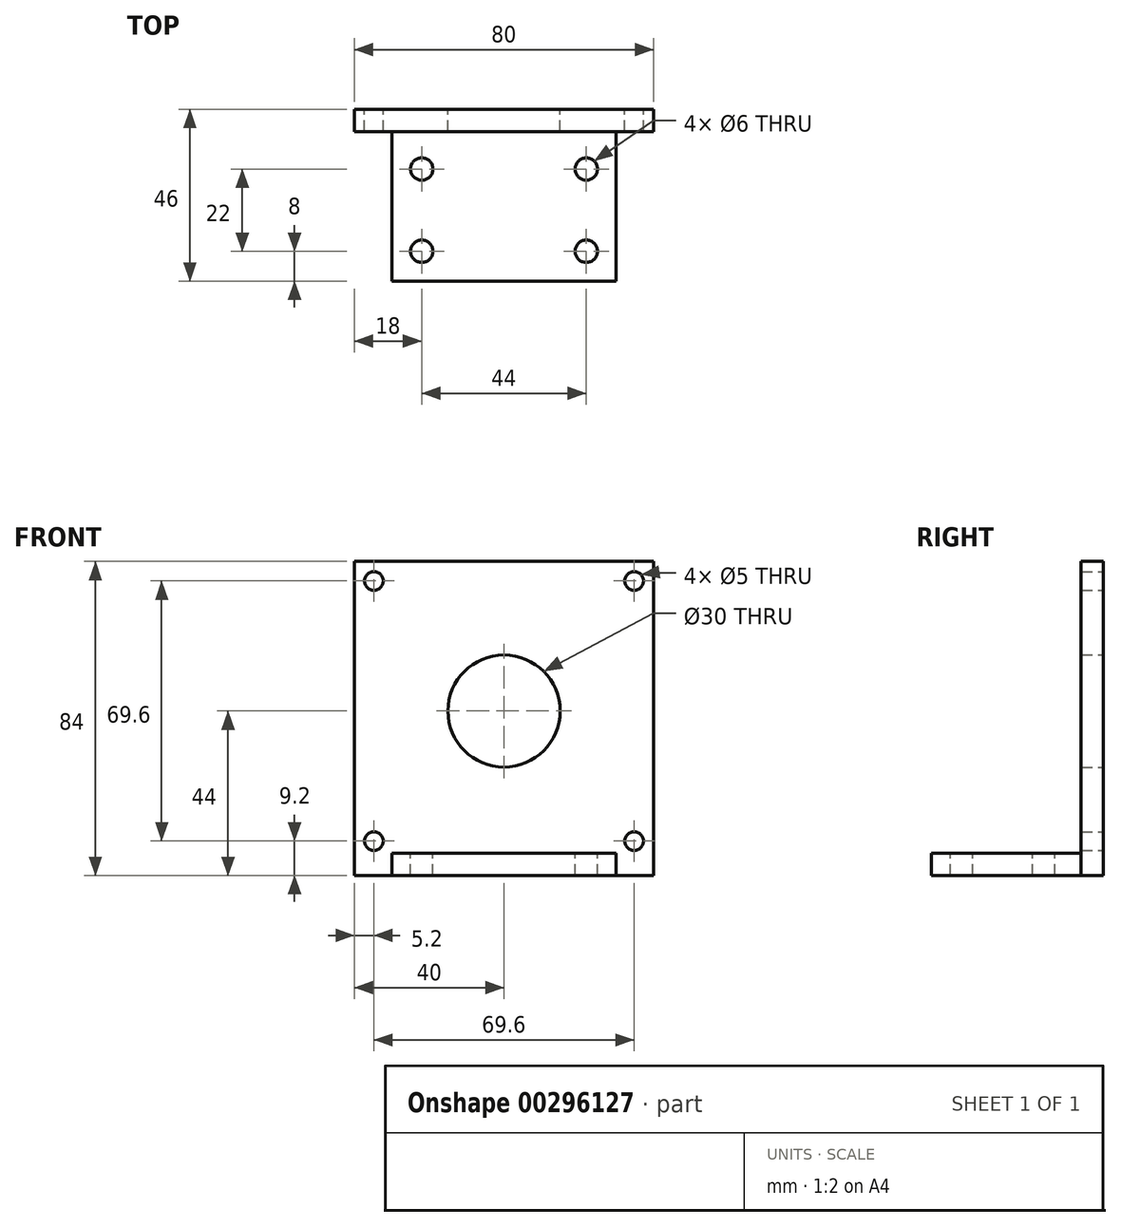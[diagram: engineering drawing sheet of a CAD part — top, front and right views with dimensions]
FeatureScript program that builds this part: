
annotation { "Feature Type Name" : "Feature", "Feature Type Description" : "" }
export const myFeature = defineFeature(function(context is Context, id is Id, definition is map)
    precondition{}
    {
        {
            var Q0;
            Q0=qCreatedBy(makeId("Front.planeOp"),FACE);
            var sketch = newSketch(context, id + "F0", { "sketchPlane" : qUnion([Q0])});
            skLineSegment(sketch, "E0.bottom", {"start": v(-40, 40) * mm, "end": v(40, 40) * mm});
            skLineSegment(sketch, "E0.top", {"start": v(-40, -40) * mm, "end": v(40, -40) * mm});
            skLineSegment(sketch, "E0.left", {"start": v(-40, 40) * mm, "end": v(-40, -40) * mm});
            skLineSegment(sketch, "E0.right", {"start": v(40, 40) * mm, "end": v(40, -40) * mm});
            skPoint(sketch, "E0.middle", {"position": v(0, 0) * mm});
            skLineSegment(sketch, "E1.bottom", {"start": v(-34.8, 34.8) * mm, "end": v(34.8, 34.8) * mm, "construction": true});
            skLineSegment(sketch, "E1.top", {"start": v(-34.8, -34.8) * mm, "end": v(34.8, -34.8) * mm, "construction": true});
            skLineSegment(sketch, "E1.left", {"start": v(-34.8, 34.8) * mm, "end": v(-34.8, -34.8) * mm, "construction": true});
            skLineSegment(sketch, "E1.right", {"start": v(34.8, 34.8) * mm, "end": v(34.8, -34.8) * mm, "construction": true});
            skCircle(sketch, "E2", {"center": v(-34.8, 34.8) * mm, "radius": 2.5 * mm});
            skCircle(sketch, "E3", {"center": v(34.8, 34.8) * mm, "radius": 2.5 * mm});
            skCircle(sketch, "E4", {"center": v(34.8, -34.8) * mm, "radius": 2.5 * mm});
            skCircle(sketch, "E5", {"center": v(-34.8, -34.8) * mm, "radius": 2.5 * mm});
            skCircle(sketch, "E6", {"center": v(0, 0) * mm, "radius": 15 * mm});
            skSolve(sketch);
        }
        {
            var Q0;
            Q0=qSketchRegion(id+"F0",true);
            extrude(context, id + "F1", {"entities" : qUnion([Q0]), "depth" : 6 * mm, "offsetDistance" : 25 * mm});
        }
        {
            var Q0;
            Q0=makeQuery(id+"F1.opExtrude","CAP_FACE",FACE,{"disambiguationData":[OSD([sQuery(id+"F0.wireOp",EDGE,"E0.bottom"),sQuery(id+"F0.wireOp",EDGE,"E0.top"),sQuery(id+"F0.wireOp",EDGE,"E0.left"),sQuery(id+"F0.wireOp",EDGE,"E0.right"),sQuery(id+"F0.wireOp",EDGE,"E2"),sQuery(id+"F0.wireOp",EDGE,"E3"),sQuery(id+"F0.wireOp",EDGE,"E4"),sQuery(id+"F0.wireOp",EDGE,"E5"),sQuery(id+"F0.wireOp",EDGE,"E6")])],"isStart":false});
            var sketch = newSketch(context, id + "F2", { "sketchPlane" : qUnion([Q0])});
            skLineSegment(sketch, "E7.bottom", {"start": v(-30, -38) * mm, "end": v(30, -38) * mm});
            skLineSegment(sketch, "E7.top", {"start": v(-30, -44) * mm, "end": v(30, -44) * mm});
            skLineSegment(sketch, "E7.left", {"start": v(-30, -38) * mm, "end": v(-30, -44) * mm});
            skLineSegment(sketch, "E7.right", {"start": v(30, -38) * mm, "end": v(30, -44) * mm});
            skSolve(sketch);
        }
        {
            var Q0;
            Q0=makeQuery(id+"F2.imprint","IMPRINT",FACE,{"disambiguationData":[TD([[makeQuery(id+"F2.imprint","IMPRINT",EDGE,{"derivedFrom":sQuery(id+"F2.wireOp",EDGE,"E7.bottom")}),-1.0]])]});
            var Q1;
            {var subQ0=sQuery(id+"F2.wireOp",EDGE,"E7.top");Q1=makeQuery(id+"F2.imprint","IMPRINT",FACE,{"disambiguationData":[TD([[makeQuery(id+"F2.imprint","IMPRINT",EDGE,{"derivedFrom":subQ0}),1.0]])]});}
            extrude(context, id + "F3", {"entities" : qUnion([Q0, Q1]), "operationType" : NewBodyOperationType.ADD, "depth" : 40 * mm, "offsetDistance" : 25 * mm});
        }
        {
            var Q0;
            Q0=makeQuery(id+"F3.opExtrude","SWEPT_FACE",FACE,{"disambiguationData":[OSD([sQuery(id+"F2.wireOp",EDGE,"E7.bottom")])]});
            var sketch = newSketch(context, id + "F4", { "sketchPlane" : qUnion([Q0])});
            skLineSegment(sketch, "E8.bottom", {"start": v(-22, -38) * mm, "end": v(22, -38) * mm, "construction": true});
            skLineSegment(sketch, "E8.top", {"start": v(-22, -16) * mm, "end": v(22, -16) * mm, "construction": true});
            skLineSegment(sketch, "E8.left", {"start": v(-22, -38) * mm, "end": v(-22, -16) * mm, "construction": true});
            skLineSegment(sketch, "E8.right", {"start": v(22, -38) * mm, "end": v(22, -16) * mm, "construction": true});
            skCircle(sketch, "E9", {"center": v(-22, -38) * mm, "radius": 3 * mm});
            skCircle(sketch, "E10", {"center": v(-22, -16) * mm, "radius": 3 * mm});
            skCircle(sketch, "E11", {"center": v(22, -16) * mm, "radius": 3 * mm});
            skCircle(sketch, "E12", {"center": v(22, -38) * mm, "radius": 3 * mm});
            skSolve(sketch);
        }
        {
            var Q0;
            Q0=qSketchRegion(id+"F4",true);
            extrude(context, id + "F5", {"entities" : qUnion([Q0]), "operationType" : NewBodyOperationType.REMOVE, "endBound" : BoundingType.UP_TO_NEXT, "oppositeDirection" : true, "depth" : 25 * mm, "offsetDistance" : 25 * mm});
        }
        {
            var Q0;
            Q0=makeQuery(id+"F1.opExtrude","CAP_FACE",FACE,{"disambiguationData":[OSD([sQuery(id+"F0.wireOp",EDGE,"E0.bottom"),sQuery(id+"F0.wireOp",EDGE,"E0.top"),sQuery(id+"F0.wireOp",EDGE,"E0.left"),sQuery(id+"F0.wireOp",EDGE,"E0.right"),sQuery(id+"F0.wireOp",EDGE,"E2"),sQuery(id+"F0.wireOp",EDGE,"E3"),sQuery(id+"F0.wireOp",EDGE,"E4"),sQuery(id+"F0.wireOp",EDGE,"E5"),sQuery(id+"F0.wireOp",EDGE,"E6")])],"isStart":false});
            var sketch = newSketch(context, id + "F6", { "sketchPlane" : qUnion([Q0])});
            skLineSegment(sketch, "E13.bottom", {"start": v(-40, -40) * mm, "end": v(40, -40) * mm});
            skLineSegment(sketch, "E13.top", {"start": v(-40, -44) * mm, "end": v(40, -44) * mm});
            skLineSegment(sketch, "E13.left", {"start": v(-40, -40) * mm, "end": v(-40, -44) * mm});
            skLineSegment(sketch, "E13.right", {"start": v(40, -40) * mm, "end": v(40, -44) * mm});
            skSolve(sketch);
        }
        {
            var Q0;
            Q0 = qSketchRegion(id + "F6", true);
            var Q1;
            Q1=makeQuery(id+"F1.opExtrude","CAP_FACE",FACE,{"disambiguationData":[OSD([sQuery(id+"F0.wireOp",EDGE,"E0.bottom"),sQuery(id+"F0.wireOp",EDGE,"E0.top"),sQuery(id+"F0.wireOp",EDGE,"E0.left"),sQuery(id+"F0.wireOp",EDGE,"E0.right"),sQuery(id+"F0.wireOp",EDGE,"E2"),sQuery(id+"F0.wireOp",EDGE,"E3"),sQuery(id+"F0.wireOp",EDGE,"E4"),sQuery(id+"F0.wireOp",EDGE,"E5"),sQuery(id+"F0.wireOp",EDGE,"E6")])],"isStart":true});
            extrude(context, id + "F7", {"entities" : qUnion([Q0]), "operationType" : NewBodyOperationType.ADD, "endBound" : BoundingType.UP_TO_SURFACE, "oppositeDirection" : true, "depth" : 25 * mm, "endBoundEntityFace" : qUnion([Q1]), "offsetDistance" : 25 * mm});
        }
    });
